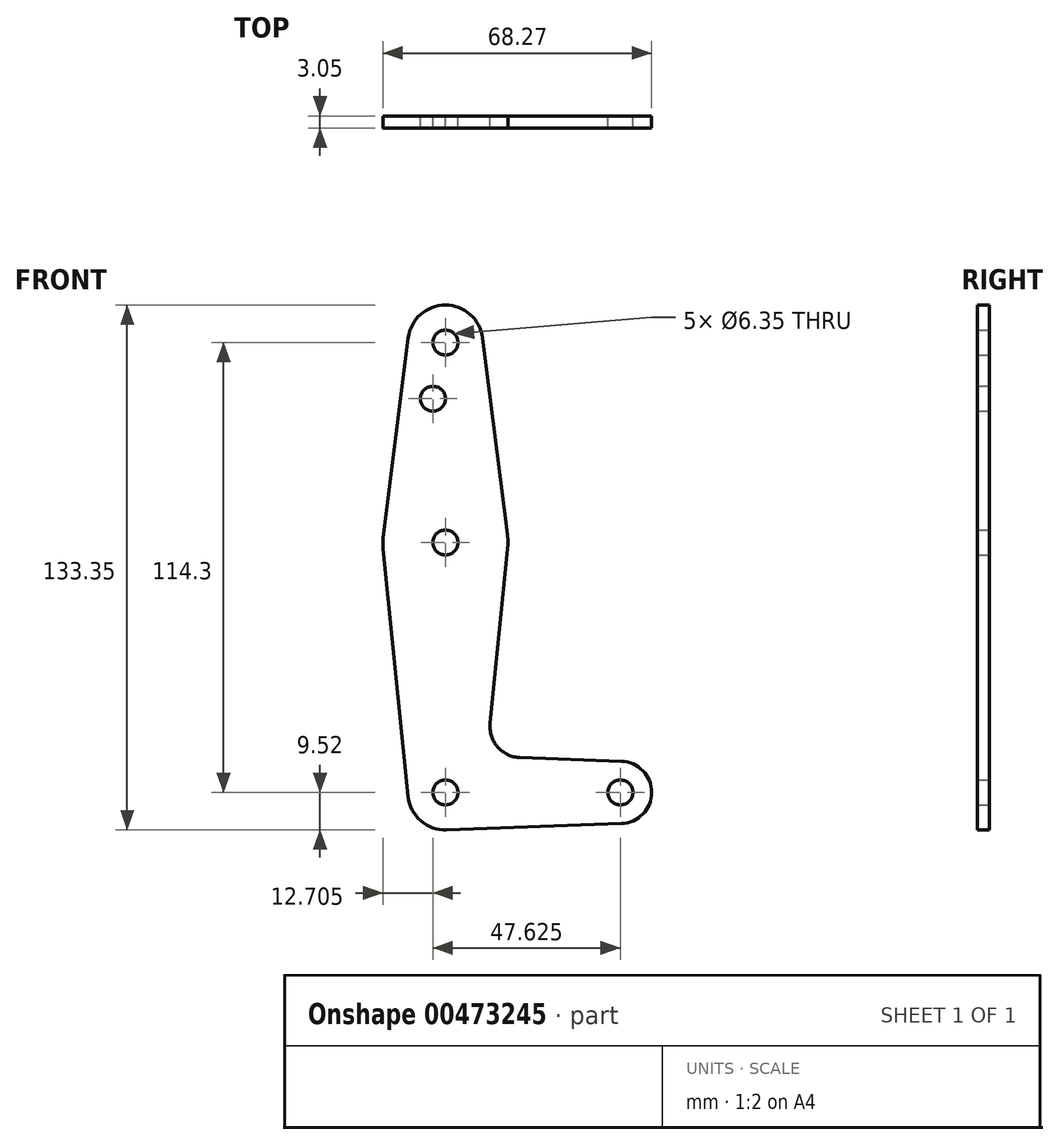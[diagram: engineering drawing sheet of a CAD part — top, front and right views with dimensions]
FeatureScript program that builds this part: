
annotation { "Feature Type Name" : "Feature", "Feature Type Description" : "" }
export const myFeature = defineFeature(function(context is Context, id is Id, definition is map)
    precondition{}
    {
        {
            var Q0;
            Q0=qCreatedBy(makeId("Front.planeOp"),FACE);
            var sketch = newSketch(context, id + "F0", { "sketchPlane" : qUnion([Q0])});
            skLineSegment(sketch, "E0", {"start": v(0, 114.3) * mm, "end": v(0, 0) * mm, "construction": true});
            skLineSegment(sketch, "E1", {"start": v(0, 0) * mm, "end": v(44.45, 0) * mm, "construction": true});
            skCircle(sketch, "E2", {"center": v(0, 114.3) * mm, "radius": 9.53 * mm});
            skCircle(sketch, "E3", {"center": v(0, 0) * mm, "radius": 9.53 * mm});
            skCircle(sketch, "E4", {"center": v(44.45, 0) * mm, "radius": 7.94 * mm});
            skCircle(sketch, "E5", {"center": v(0, 63.5) * mm, "radius": 15.88 * mm});
            skLineSegment(sketch, "E6", {"start": v(-9.45, 115.5) * mm, "end": v(-15.75, 65.48) * mm});
            skLineSegment(sketch, "E7", {"start": v(9.45, 115.5) * mm, "end": v(15.75, 65.48) * mm});
            skLineSegment(sketch, "E8", {"start": v(-15.8, 61.91) * mm, "end": v(-9.48, -0.95) * mm});
            skLineSegment(sketch, "E9", {"start": v(15.8, 61.91) * mm, "end": v(11.34, 17.6) * mm});
            skCircle(sketch, "E10", {"center": v(0, 114.3) * mm, "radius": 3.18 * mm});
            skCircle(sketch, "E11", {"center": v(-3.18, 100.03) * mm, "radius": 3.18 * mm});
            skCircle(sketch, "E12", {"center": v(0, 63.5) * mm, "radius": 3.18 * mm});
            skCircle(sketch, "E13", {"center": v(0, 0) * mm, "radius": 3.18 * mm});
            skCircle(sketch, "E14", {"center": v(44.45, 0) * mm, "radius": 3.18 * mm});
            skLineSegment(sketch, "E15", {"start": v(18.97, 8.85) * mm, "end": v(44.73, 7.93) * mm});
            skLineSegment(sketch, "E16", {"start": v(0.34, -9.52) * mm, "end": v(44.73, -7.93) * mm});
            skArc(sketch, "E17.filletArc", {"start": v(11.34, 17.6) * mm, "mid": v(13.26, 11.57) * mm, "end": v(18.97, 8.85) * mm});
            skSolve(sketch);
        }
        {
            var Q0;
            Q0 = qSketchRegion(id + "F0", true);
            extrude(context, id + "F1", {"entities" : qUnion([Q0]), "depth" : 3.05 * mm});
        }
    });
